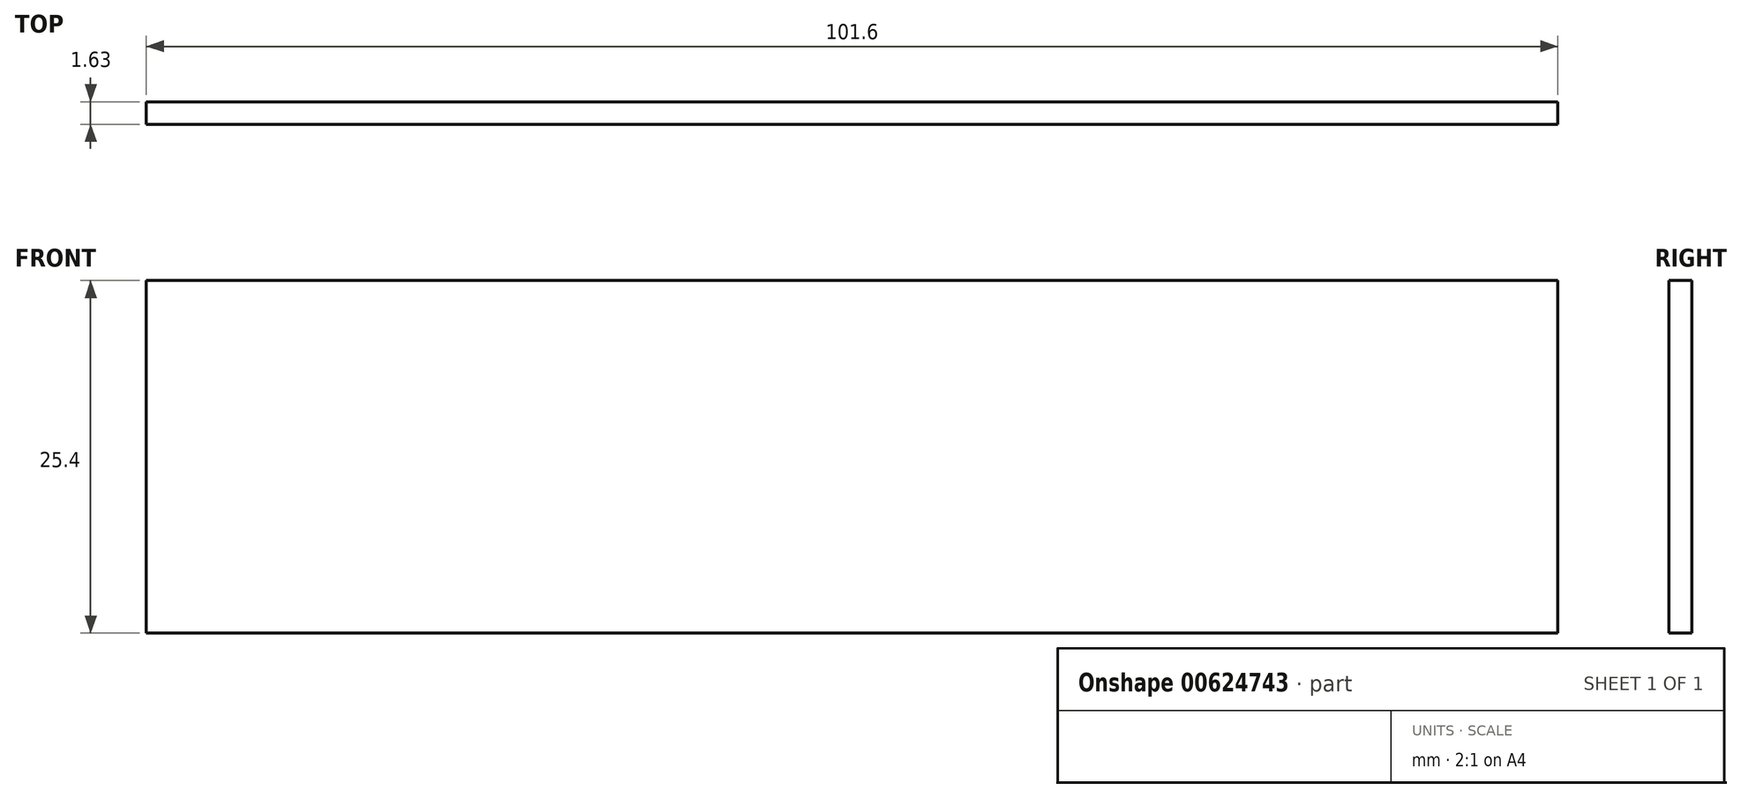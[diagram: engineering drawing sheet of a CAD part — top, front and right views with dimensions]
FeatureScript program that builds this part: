
annotation { "Feature Type Name" : "Feature", "Feature Type Description" : "" }
export const myFeature = defineFeature(function(context is Context, id is Id, definition is map)
    precondition{}
    {
        {
            var Q0;
            Q0=qCreatedBy(makeId("Top.planeOp"),FACE);
            var sketch = newSketch(context, id + "F0", { "sketchPlane" : qUnion([Q0])});
            skLineSegment(sketch, "E0.bottom", {"start": v(0, 0) * mm, "end": v(101.6, 0) * mm});
            skLineSegment(sketch, "E0.top", {"start": v(0, 1.63) * mm, "end": v(101.6, 1.63) * mm});
            skLineSegment(sketch, "E0.left", {"start": v(0, 0) * mm, "end": v(0, 1.63) * mm});
            skLineSegment(sketch, "E0.right", {"start": v(101.6, 0) * mm, "end": v(101.6, 1.63) * mm});
            skSolve(sketch);
        }
        {
            var Q0;
            Q0=makeQuery(id+"F0.imprint","IMPRINT",FACE,{"disambiguationData":[TD([[makeQuery(id+"F0.imprint","IMPRINT",EDGE,{"derivedFrom":sQuery(id+"F0.wireOp",EDGE,"E0.bottom")}),1.0]])]});
            extrude(context, id + "F1", {"entities" : qUnion([Q0]), "depth" : 25.4 * mm, "offsetDistance" : 25.4 * mm});
        }
    });
